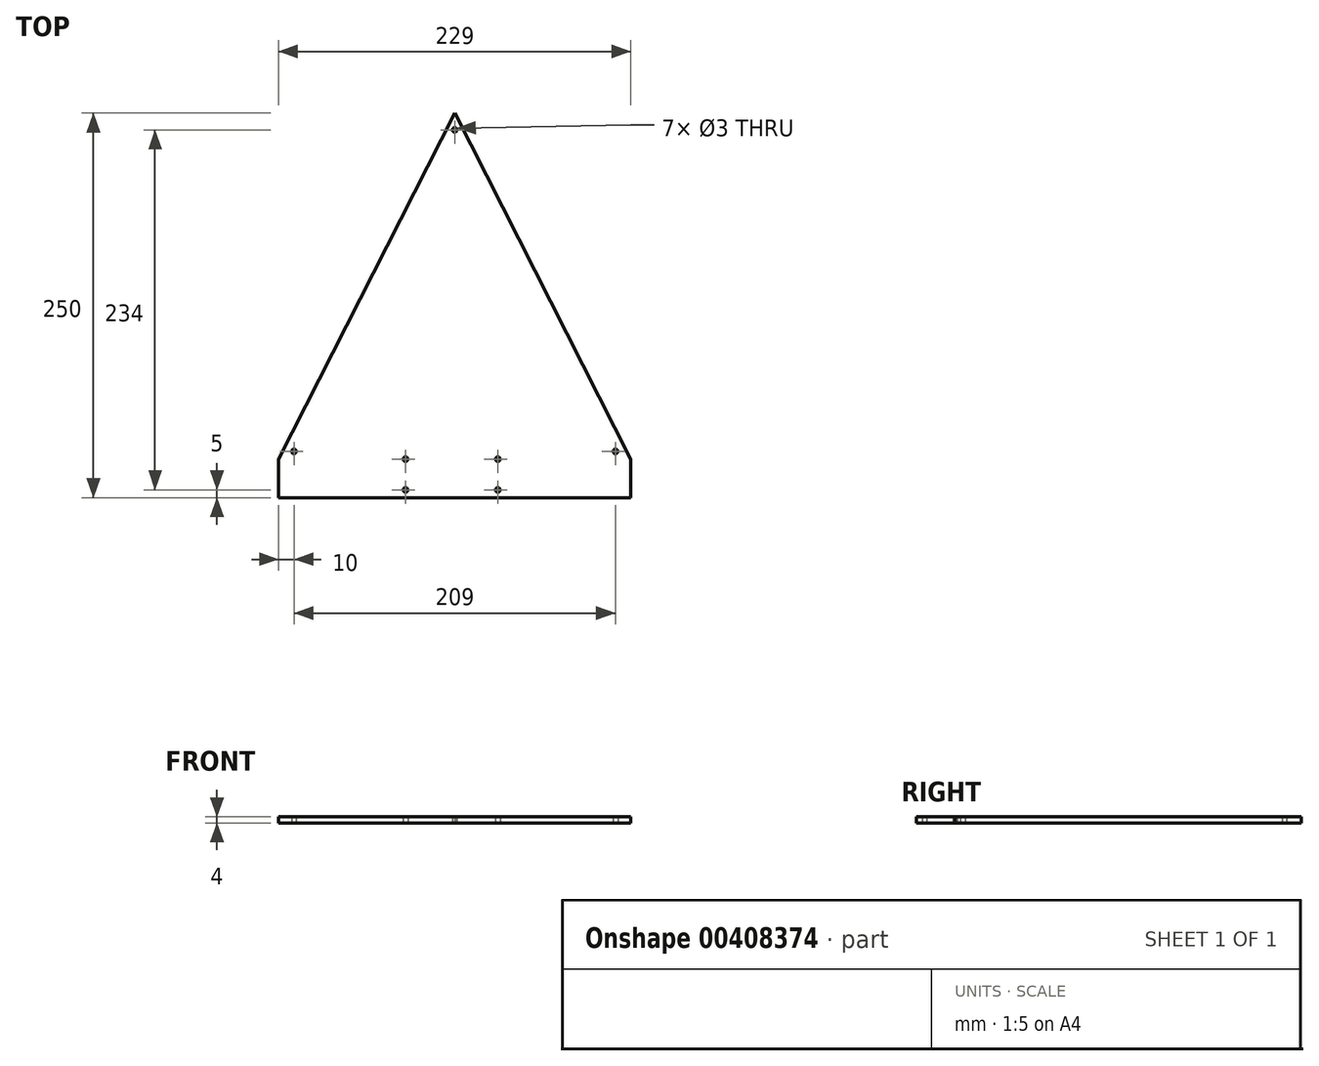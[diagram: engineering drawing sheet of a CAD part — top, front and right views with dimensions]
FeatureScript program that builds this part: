
annotation { "Feature Type Name" : "Feature", "Feature Type Description" : "" }
export const myFeature = defineFeature(function(context is Context, id is Id, definition is map)
    precondition{}
    {
        {
            var Q0;
            Q0=qCreatedBy(makeId("Top.planeOp"),FACE);
            var sketch = newSketch(context, id + "F0", { "sketchPlane" : qUnion([Q0])});
            skPoint(sketch, "E0", {"position": v(-114.5, 214) * mm});
            skPoint(sketch, "E1", {"position": v(-10, 5) * mm});
            skPoint(sketch, "E2", {"position": v(-219, 5) * mm});
            skPoint(sketch, "E3", {"position": v(-146.5, 0) * mm});
            skPoint(sketch, "E4", {"position": v(-146.5, -20) * mm});
            skPoint(sketch, "E5", {"position": v(-86.5, 0) * mm});
            skPoint(sketch, "E6", {"position": v(-86.5, -20) * mm});
            skLineSegment(sketch, "E7", {"start": v(-114.5, 225) * mm, "end": v(0, 0) * mm});
            skLineSegment(sketch, "E8", {"start": v(-229, 0) * mm, "end": v(-114.5, 225) * mm});
            skLineSegment(sketch, "E9", {"start": v(-229, 0) * mm, "end": v(-229, -25) * mm});
            skLineSegment(sketch, "E10", {"start": v(-229, -25) * mm, "end": v(0, -25) * mm});
            skLineSegment(sketch, "E11", {"start": v(0, -25) * mm, "end": v(0, 0) * mm});
            skSolve(sketch);
        }
        {
            var Q0;
            Q0=makeQuery(id+"F0.imprint","IMPRINT",FACE,{"disambiguationData":[TD([[makeQuery(id+"F0.imprint","IMPRINT",EDGE,{"derivedFrom":sQuery(id+"F0.wireOp",EDGE,"E7")}),-1.0]])]});
            extrude(context, id + "F1", {"entities" : qUnion([Q0]), "depth" : 4 * mm});
        }
        {
            var Q0;
            Q0=sQuery(id+"F0.wireOp",VERTEX,"E0");
            var Q1;
            Q1=sQuery(id+"F0.wireOp",VERTEX,"E2");
            var Q2;
            Q2=sQuery(id+"F0.wireOp",VERTEX,"E3");
            var Q3;
            Q3=sQuery(id+"F0.wireOp",VERTEX,"E4");
            var Q4;
            Q4=sQuery(id+"F0.wireOp",VERTEX,"E6");
            var Q5;
            Q5=sQuery(id+"F0.wireOp",VERTEX,"E5");
            var Q6;
            Q6=sQuery(id+"F0.wireOp",VERTEX,"E1");
            var Q7;
            Q7=makeQuery(id+"F1.opExtrude","SWEPT_BODY",BODY,{"disambiguationData":[OSD([sQuery(id+"F0.wireOp",EDGE,"E7"),sQuery(id+"F0.wireOp",EDGE,"E8"),sQuery(id+"F0.wireOp",EDGE,"E9"),sQuery(id+"F0.wireOp",EDGE,"E10"),sQuery(id+"F0.wireOp",EDGE,"E11")])]});
            hole(context, id + "F2", {"style" : HoleStyle.SIMPLE, "endStyle" : HoleEndStyle.THROUGH, "oppositeDirection" : true, "holeDiameter" : 3 * mm, "tappedDepth" : 12 * mm, "tapClearance" : 3, "locations" : qUnion([Q0, Q1, Q2, Q3, Q4, Q5, Q6]), "scope" : qUnion([Q7])});
        }
    });
